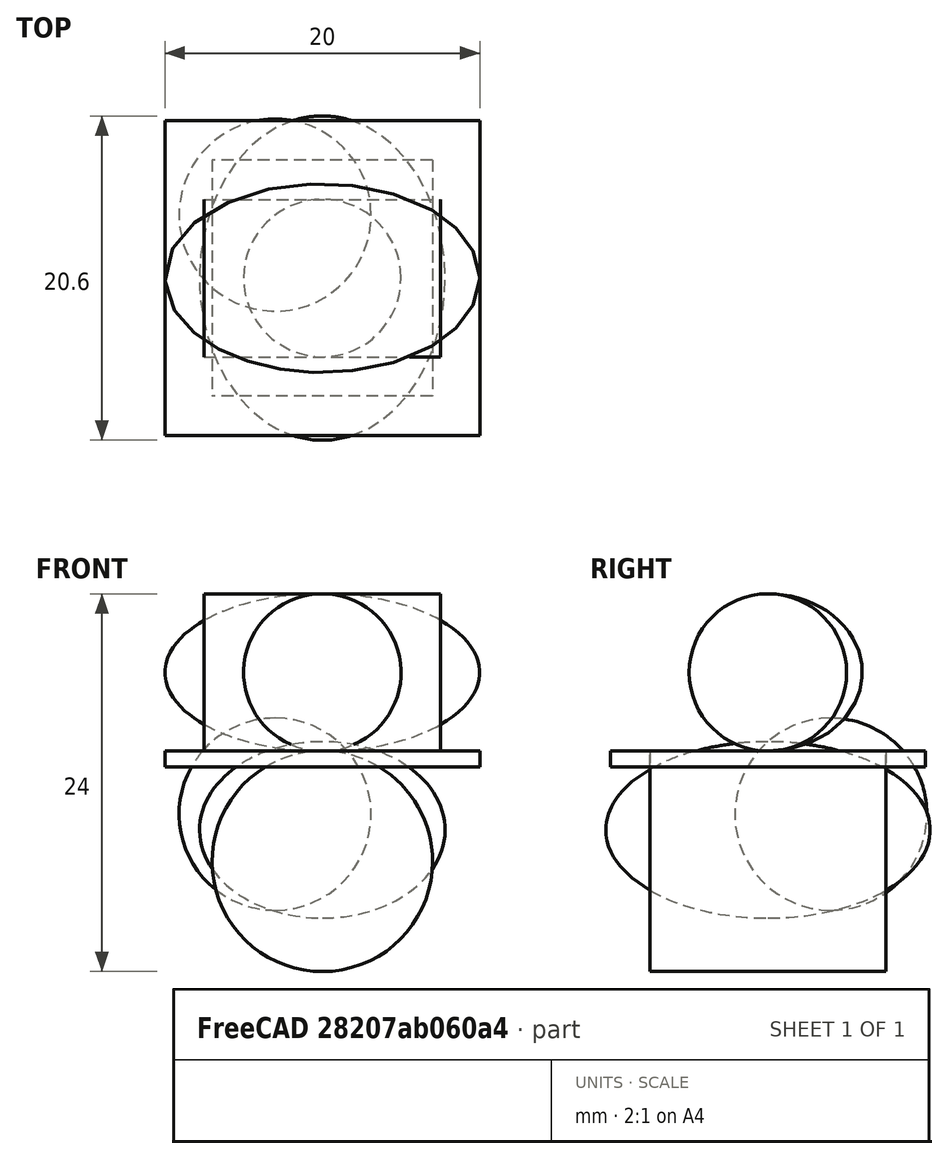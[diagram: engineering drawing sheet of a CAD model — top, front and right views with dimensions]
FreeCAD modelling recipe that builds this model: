
FCSTD DOCUMENT  (FreeCAD 0.18R4 (GitTag))
Label: CAD
License: All rights reserved
LicenseURL: http://en.wikipedia.org/wiki/All_rights_reserved
objects: Part::Sphere×2, Part::Cylinder×2, Part::Ellipsoid×2, Part::Box×1
note: 7 computed .brp shape members not serialized (recipe doc carries the construction recipe); baked Part::Feature solids carry a one-line shape summary decoded from their .brp

FEATURE [Part::Sphere] Sphere
  Angle1 = -90
  Angle2 = 90
  Angle3 = 360
  AttacherType = Attacher::AttachEngine3D
  Radius = 5
FEATURE [Part::Box] Box  label="Cube"
  AttacherType = Attacher::AttachEngine3D
  Height = 1
  Length = 20
  Placement = pos=(-10,-10,-6) rot=(0,0,1;0rad)
  Width = 20
FEATURE [Part::Sphere] Sphere001
  Angle1 = -90
  Angle2 = 90
  Angle3 = 360
  AttacherType = Attacher::AttachEngine3D
  Placement = pos=(-3,4,-9) rot=(0,0,1;0rad)
  Radius = 6.1
FEATURE [Part::Cylinder] Cylinder
  Angle = 360
  AttacherType = Attacher::AttachEngine3D
  Height = 15
  Placement = pos=(-7.5,0,0) rot=(0,1,0;1.5708rad)
  Radius = 5
FEATURE [Part::Cylinder] Cylinder001
  Angle = 360
  AttacherType = Attacher::AttachEngine3D
  Height = 15
  Placement = pos=(0,7.5,-12) rot=(1,0,0;1.5708rad)
  Radius = 7
FEATURE [Part::Ellipsoid] Ellipsoid
  Angle1 = -90
  Angle2 = 90
  Angle3 = 360
  AttacherType = Attacher::AttachEngine3D
  Radius1 = 5
  Radius2 = 10
  Radius3 = 6
FEATURE [Part::Ellipsoid] Ellipsoid001
  Angle1 = -90
  Angle2 = 90
  Angle3 = 360
  AttacherType = Attacher::AttachEngine3D
  Placement = pos=(0,0,-10) rot=(0,0,1;1.5708rad)
  Radius1 = 5.6
  Radius2 = 10.3
  Radius3 = 7.8
